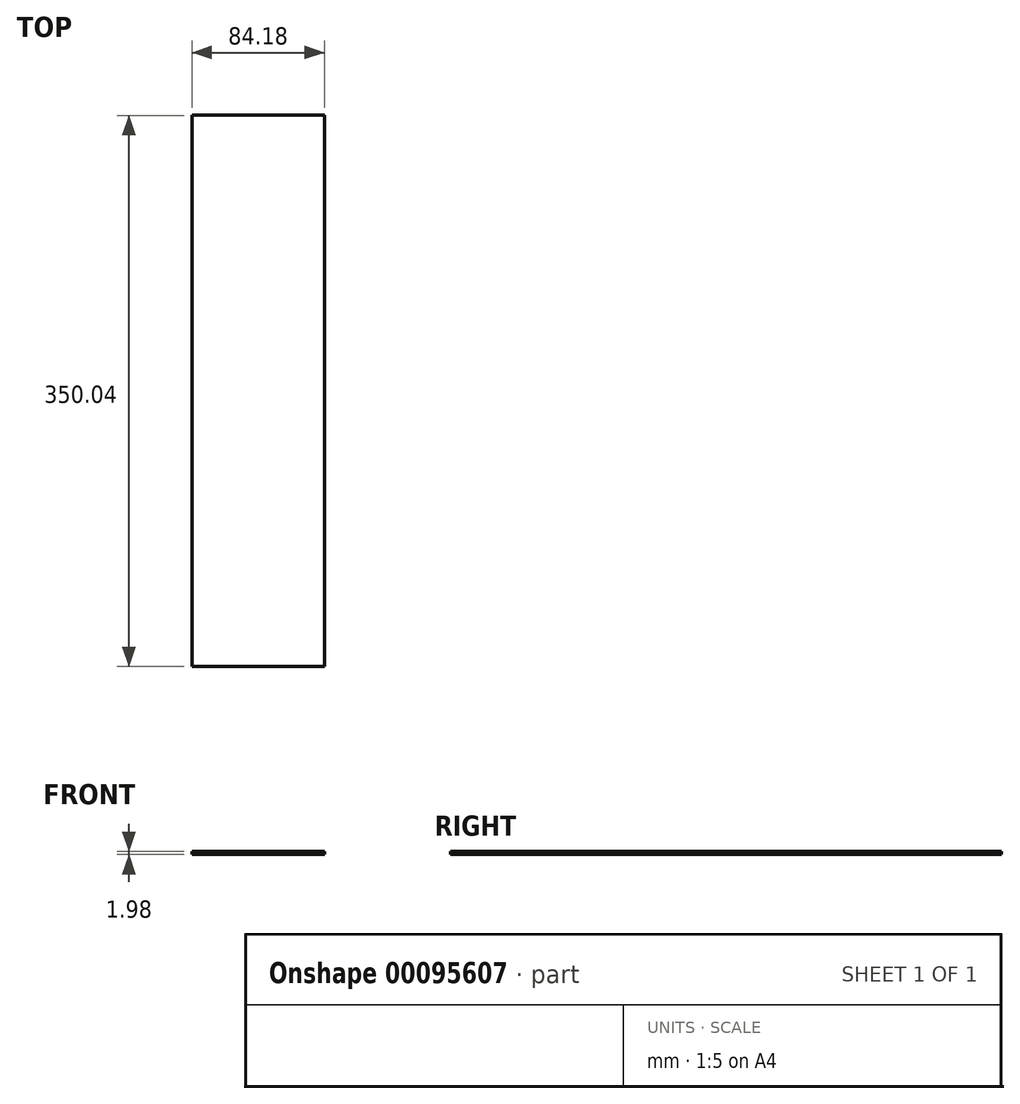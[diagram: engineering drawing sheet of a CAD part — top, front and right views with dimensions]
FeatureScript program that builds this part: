
annotation { "Feature Type Name" : "Feature", "Feature Type Description" : "" }
export const myFeature = defineFeature(function(context is Context, id is Id, definition is map)
    precondition{}
    {
        {
            var Q0;
            Q0=qCreatedBy(makeId("Top.planeOp"),FACE);
            var sketch = newSketch(context, id + "F0", { "sketchPlane" : qUnion([Q0])});
            skLineSegment(sketch, "E0.bottom", {"start": v(-42.09, -175.02) * mm, "end": v(42.09, -175.02) * mm});
            skLineSegment(sketch, "E0.top", {"start": v(-42.09, 175.02) * mm, "end": v(42.09, 175.02) * mm});
            skLineSegment(sketch, "E0.left", {"start": v(-42.09, -175.02) * mm, "end": v(-42.09, 175.02) * mm});
            skLineSegment(sketch, "E0.right", {"start": v(42.09, -175.02) * mm, "end": v(42.09, 175.02) * mm});
            skPoint(sketch, "E0.middle", {"position": v(0, 0) * mm});
            skSolve(sketch);
        }
        {
            var Q0;
            Q0=makeQuery(id+"F0.imprint","IMPRINT",FACE,{"disambiguationData":[TD([[makeQuery(id+"F0.imprint","IMPRINT",EDGE,{"derivedFrom":sQuery(id+"F0.wireOp",EDGE,"E0.bottom")}),1.0]])]});
            extrude(context, id + "F1", {"entities" : qUnion([Q0]), "depth" : 1.98 * mm});
        }
    });
